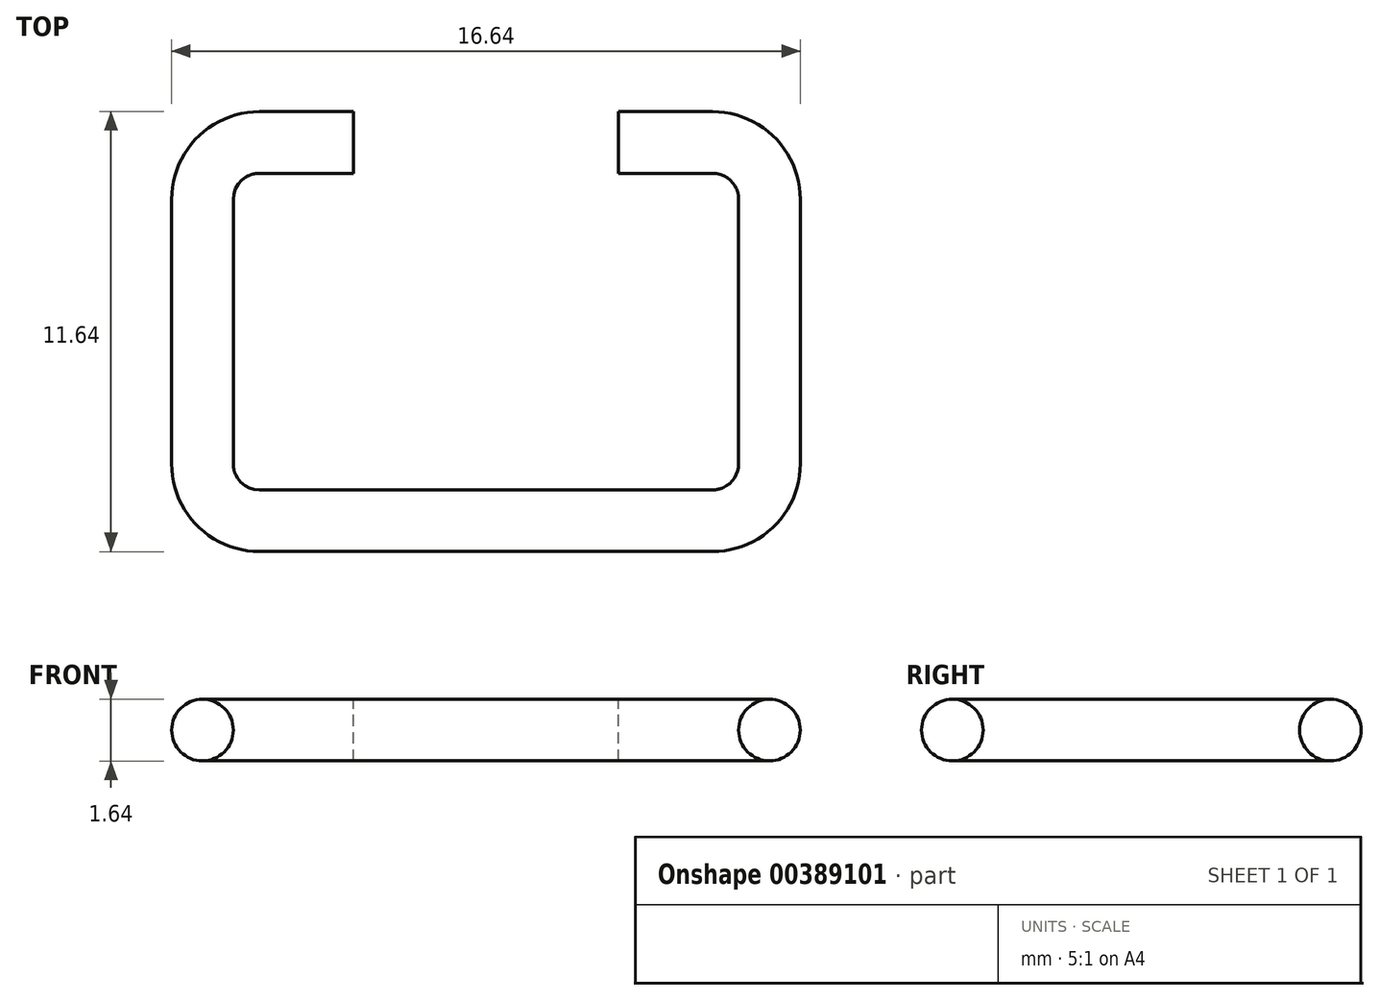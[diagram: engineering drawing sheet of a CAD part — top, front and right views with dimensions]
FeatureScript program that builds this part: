
annotation { "Feature Type Name" : "Feature", "Feature Type Description" : "" }
export const myFeature = defineFeature(function(context is Context, id is Id, definition is map)
    precondition{}
    {
        {
            var Q0;
            Q0=qCreatedBy(makeId("Top.planeOp"),FACE);
            var sketch = newSketch(context, id + "F0", { "sketchPlane" : qUnion([Q0])});
            skLineSegment(sketch, "E0.bottom", {"start": v(6, 5) * mm, "end": v(-6, 5) * mm, "construction": true});
            skLineSegment(sketch, "E0.top", {"start": v(6, -5) * mm, "end": v(-6, -5) * mm, "construction": true});
            skLineSegment(sketch, "E0.left", {"start": v(7.5, 3.5) * mm, "end": v(7.5, -3.5) * mm, "construction": true});
            skLineSegment(sketch, "E0.right", {"start": v(-7.5, 3.5) * mm, "end": v(-7.5, -3.5) * mm, "construction": true});
            skPoint(sketch, "E0.middle", {"position": v(0, 0) * mm});
            skPoint(sketch, "E1.visualSharp", {"position": v(-7.5, 5) * mm});
            skArc(sketch, "E1.filletArc", {"start": v(-6, 5) * mm, "mid": v(-7.06, 4.56) * mm, "end": v(-7.5, 3.5) * mm, "construction": true});
            skPoint(sketch, "E2.visualSharp", {"position": v(7.5, 5) * mm});
            skArc(sketch, "E2.filletArc", {"start": v(7.5, 3.5) * mm, "mid": v(7.06, 4.56) * mm, "end": v(6, 5) * mm, "construction": true});
            skPoint(sketch, "E3.visualSharp", {"position": v(7.5, -5) * mm});
            skArc(sketch, "E3.filletArc", {"start": v(6, -5) * mm, "mid": v(7.06, -4.56) * mm, "end": v(7.5, -3.5) * mm, "construction": true});
            skPoint(sketch, "E4.visualSharp", {"position": v(-7.5, -5) * mm});
            skArc(sketch, "E4.filletArc", {"start": v(-7.5, -3.5) * mm, "mid": v(-7.06, -4.56) * mm, "end": v(-6, -5) * mm, "construction": true});
            skLineSegment(sketch, "E5", {"start": v(-3.5, 7.5) * mm, "end": v(-3.5, 2.5) * mm, "construction": true});
            skLineSegment(sketch, "E6.MirrorCS", {"start": v(3.5, 7.5) * mm, "end": v(3.5, 2.5) * mm, "construction": true});
            skLineSegment(sketch, "E7", {"start": v(-3.5, 5) * mm, "end": v(-6, 5) * mm});
            skLineSegment(sketch, "E8", {"start": v(-7.5, 3.5) * mm, "end": v(-7.5, -3.5) * mm});
            skLineSegment(sketch, "E9", {"start": v(-6, -5) * mm, "end": v(6, -5) * mm});
            skLineSegment(sketch, "E10", {"start": v(7.5, -3.5) * mm, "end": v(7.5, 3.5) * mm});
            skLineSegment(sketch, "E11", {"start": v(6, 5) * mm, "end": v(3.5, 5) * mm});
            skArc(sketch, "E12", {"start": v(-6, 5) * mm, "mid": v(-7.06, 4.56) * mm, "end": v(-7.5, 3.5) * mm});
            skArc(sketch, "E13", {"start": v(-6, -5) * mm, "mid": v(-7.06, -4.56) * mm, "end": v(-7.5, -3.5) * mm});
            skArc(sketch, "E14", {"start": v(6, -5) * mm, "mid": v(7.06, -4.56) * mm, "end": v(7.5, -3.5) * mm});
            skArc(sketch, "E15", {"start": v(7.5, 3.5) * mm, "mid": v(7.06, 4.56) * mm, "end": v(6, 5) * mm});
            skSolve(sketch);
        }
        {
            var Q0;
            Q0=qCreatedBy(makeId("Top.planeOp"),FACE);
            var sketch = newSketch(context, id + "F1", { "sketchPlane" : qUnion([Q0])});
            skLineSegment(sketch, "E16", {"start": v(-3.5, 5) * mm, "end": v(-6, 5) * mm});
            skArc(sketch, "E17", {"start": v(-6, 5) * mm, "mid": v(-7.06, 4.56) * mm, "end": v(-7.5, 3.5) * mm});
            skLineSegment(sketch, "E18", {"start": v(-7.5, 3.5) * mm, "end": v(-7.5, -3.5) * mm});
            skArc(sketch, "E19", {"start": v(-7.5, -3.5) * mm, "mid": v(-7.06, -4.56) * mm, "end": v(-6, -5) * mm});
            skLineSegment(sketch, "E20", {"start": v(0, -5) * mm, "end": v(-6, -5) * mm});
            skLineSegment(sketch, "E21.MirrorCS", {"start": v(3.5, 5) * mm, "end": v(6, 5) * mm});
            skArc(sketch, "E22.MirrorCS", {"start": v(6, 5) * mm, "mid": v(7.06, 4.56) * mm, "end": v(7.5, 3.5) * mm});
            skLineSegment(sketch, "E23.MirrorCS", {"start": v(7.5, 3.5) * mm, "end": v(7.5, -3.5) * mm});
            skArc(sketch, "E24.MirrorCS", {"start": v(7.5, -3.5) * mm, "mid": v(7.06, -4.56) * mm, "end": v(6, -5) * mm});
            skLineSegment(sketch, "E25.MirrorCS", {"start": v(0, -5) * mm, "end": v(6, -5) * mm});
            skSolve(sketch);
        }
        {
            var Q0;
            Q0=qCreatedBy(makeId("Right.planeOp"),FACE);
            cPlane(context, id + "F2", {"entities" : qUnion([Q0]), "cplaneType" : CPlaneType.OFFSET, "offset" : 3.5 * mm, "width" : 150 * mm, "height" : 150 * mm});
        }
        {
            var Q0;
            Q0=qCreatedBy(id+"F2.planeOp",FACE);
            var sketch = newSketch(context, id + "F3", { "sketchPlane" : qUnion([Q0])});
            skCircle(sketch, "E26", {"center": v(5, 0) * mm, "radius": 0.81 * mm});
            skSolve(sketch);
        }
        {
            var Q0;
            Q0=makeQuery(id+"F3.imprint","IMPRINT",FACE,{"disambiguationData":[TD([[makeQuery(id+"F3.imprint","IMPRINT",EDGE,{"derivedFrom":sQuery(id+"F3.wireOp",EDGE,"E26")}),1.0]])]});
            var Q1;
            Q1=sQuery(id+"F1.wireOp",EDGE,"E21.MirrorCS");
            var Q2;
            Q2=sQuery(id+"F1.wireOp",EDGE,"E22.MirrorCS");
            var Q3;
            Q3=sQuery(id+"F1.wireOp",EDGE,"E23.MirrorCS");
            var Q4;
            Q4=sQuery(id+"F1.wireOp",EDGE,"E24.MirrorCS");
            var Q5;
            Q5=sQuery(id+"F1.wireOp",EDGE,"E25.MirrorCS");
            var Q6;
            Q6=sQuery(id+"F1.wireOp",EDGE,"E20");
            var Q7;
            Q7=sQuery(id+"F1.wireOp",EDGE,"E19");
            var Q8;
            Q8=sQuery(id+"F1.wireOp",EDGE,"E18");
            var Q9;
            Q9=sQuery(id+"F1.wireOp",EDGE,"E17");
            var Q10;
            Q10=sQuery(id+"F1.wireOp",EDGE,"E16");
            sweep(context, id + "F4", {"profiles" : qUnion([Q0]), "path" : qUnion([Q1, Q2, Q3, Q4, Q5, Q6, Q7, Q8, Q9, Q10])});
        }
    });
